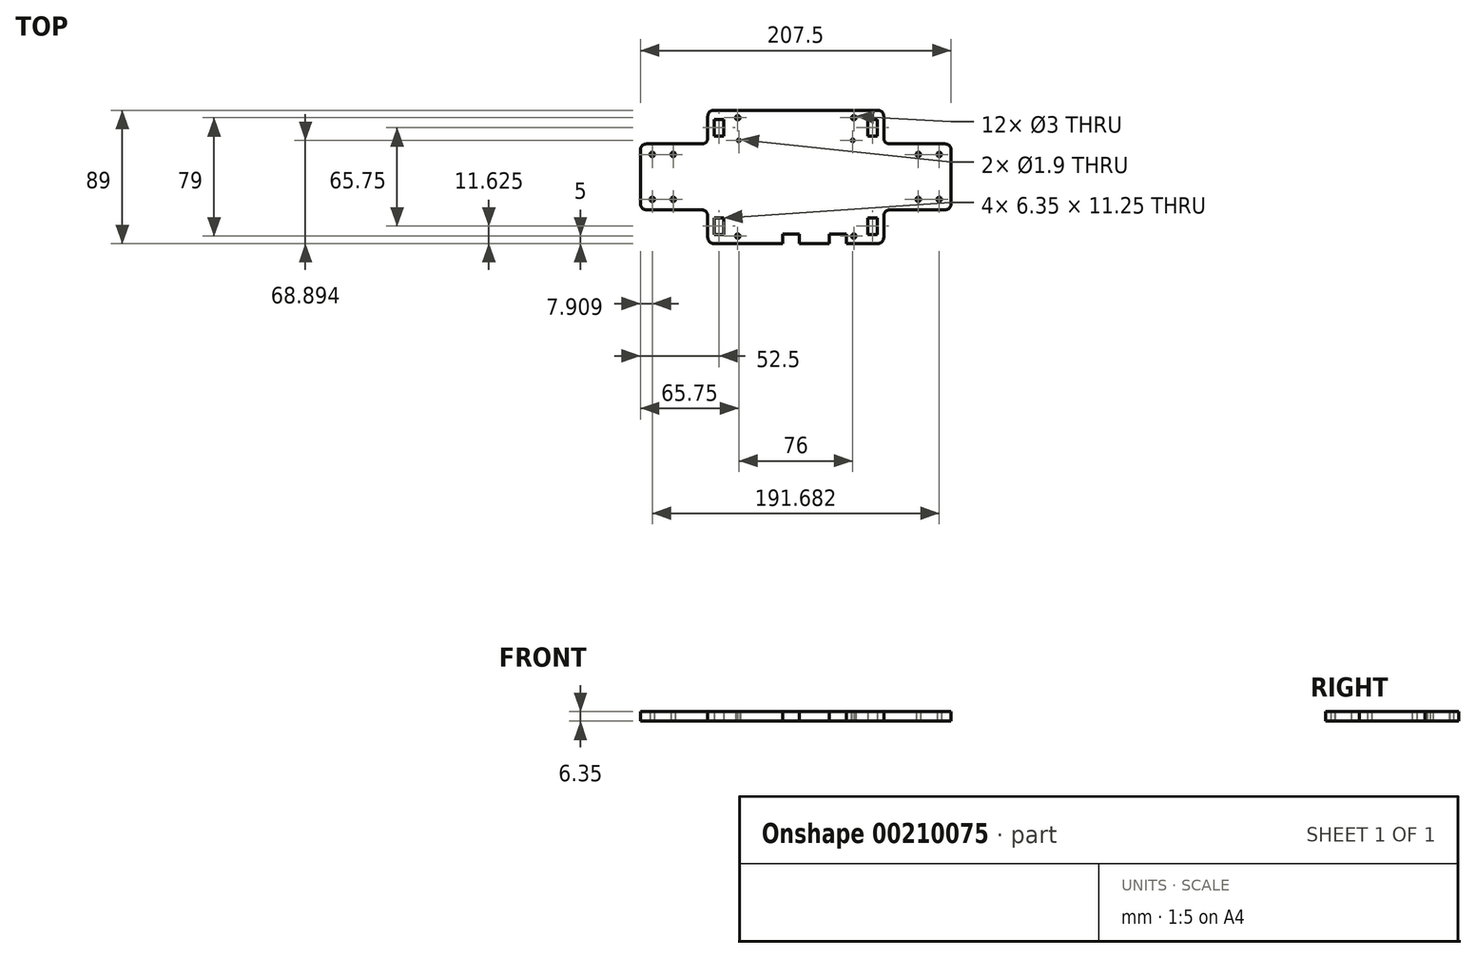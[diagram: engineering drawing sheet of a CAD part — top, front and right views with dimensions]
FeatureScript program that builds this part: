
annotation { "Feature Type Name" : "Feature", "Feature Type Description" : "" }
export const myFeature = defineFeature(function(context is Context, id is Id, definition is map)
    precondition{}
    {
        {
            var Q0;
            Q0=qCreatedBy(makeId("Top.planeOp"),FACE);
            var sketch = newSketch(context, id + "F0", { "sketchPlane" : qUnion([Q0])});
            skLineSegment(sketch, "E0.bottom", {"start": v(-54.75, 44.5) * mm, "end": v(103.75, 44.5) * mm});
            skLineSegment(sketch, "E0.top", {"start": v(-103.75, -44.5) * mm, "end": v(103.75, -44.5) * mm});
            skLineSegment(sketch, "E0.left", {"start": v(-103.75, 18) * mm, "end": v(-103.75, -44.5) * mm});
            skLineSegment(sketch, "E0.right", {"start": v(103.75, 44.5) * mm, "end": v(103.75, -44.5) * mm});
            skPoint(sketch, "E0.middle", {"position": v(0, 0) * mm});
            skLineSegment(sketch, "E1", {"start": v(-98.75, 44.5) * mm, "end": v(-98.75, -44.5) * mm});
            skLineSegment(sketch, "E2", {"start": v(-78.75, 44.5) * mm, "end": v(-78.75, -44.5) * mm});
            skLineSegment(sketch, "E3", {"start": v(-43.75, 44.5) * mm, "end": v(-43.75, -44.5) * mm});
            skLineSegment(sketch, "E4", {"start": v(43.75, 44.5) * mm, "end": v(43.75, -44.5) * mm});
            skLineSegment(sketch, "E5", {"start": v(78.75, 44.5) * mm, "end": v(78.75, -44.5) * mm});
            skLineSegment(sketch, "E6", {"start": v(98.75, 44.5) * mm, "end": v(98.75, -44.5) * mm});
            skLineSegment(sketch, "E7", {"start": v(-43.75, 31.5) * mm, "end": v(43.75, 31.5) * mm});
            skLineSegment(sketch, "E8", {"start": v(-43.75, -31.5) * mm, "end": v(43.75, -31.5) * mm});
            skLineSegment(sketch, "E9", {"start": v(-98.75, 22) * mm, "end": v(-78.75, 22) * mm});
            skLineSegment(sketch, "E10", {"start": v(-98.75, -22) * mm, "end": v(-78.75, -22) * mm});
            skLineSegment(sketch, "E11", {"start": v(78.75, 22) * mm, "end": v(98.75, 22) * mm});
            skLineSegment(sketch, "E12", {"start": v(78.75, -22) * mm, "end": v(98.75, -22) * mm});
            skPoint(sketch, "E13", {"position": v(38, 24.4) * mm});
            skPoint(sketch, "E14", {"position": v(-38, 24.4) * mm});
            skCircle(sketch, "E15", {"center": v(-38, 24.4) * mm, "radius": 0.95 * mm});
            skCircle(sketch, "E16", {"center": v(38, 24.4) * mm, "radius": 0.95 * mm});
            skPoint(sketch, "E17", {"position": v(-81.84, -15) * mm});
            skPoint(sketch, "E18", {"position": v(-81.84, 15) * mm});
            skPoint(sketch, "E19", {"position": v(-95.84, 15) * mm});
            skPoint(sketch, "E20", {"position": v(-95.84, -15) * mm});
            skPoint(sketch, "E21", {"position": v(81.84, -15) * mm});
            skPoint(sketch, "E22", {"position": v(95.84, -15) * mm});
            skPoint(sketch, "E23", {"position": v(95.84, 15) * mm});
            skPoint(sketch, "E24", {"position": v(81.84, 15) * mm});
            skCircle(sketch, "E25", {"center": v(-95.84, -15) * mm, "radius": 1.5 * mm});
            skCircle(sketch, "E26", {"center": v(-81.84, -15) * mm, "radius": 1.5 * mm});
            skCircle(sketch, "E27", {"center": v(-81.84, 15) * mm, "radius": 1.5 * mm});
            skCircle(sketch, "E28", {"center": v(-95.84, 15) * mm, "radius": 1.5 * mm});
            skCircle(sketch, "E29", {"center": v(81.84, 15) * mm, "radius": 1.5 * mm});
            skCircle(sketch, "E30", {"center": v(95.84, 15) * mm, "radius": 1.5 * mm});
            skCircle(sketch, "E31", {"center": v(95.84, -15) * mm, "radius": 1.5 * mm});
            skCircle(sketch, "E32", {"center": v(81.84, -15) * mm, "radius": 1.5 * mm});
            skLineSegment(sketch, "E33.bottom", {"start": v(-8.75, -38.15) * mm, "end": v(2.5, -38.15) * mm});
            skLineSegment(sketch, "E33.top", {"start": v(-8.75, -44.5) * mm, "end": v(2.5, -44.5) * mm});
            skLineSegment(sketch, "E33.left", {"start": v(-8.75, -38.15) * mm, "end": v(-8.75, -44.5) * mm});
            skLineSegment(sketch, "E33.right", {"start": v(2.5, -38.15) * mm, "end": v(2.5, -44.5) * mm});
            skLineSegment(sketch, "E34.bottom", {"start": v(22.5, -44.5) * mm, "end": v(33.75, -44.5) * mm});
            skLineSegment(sketch, "E34.top", {"start": v(22.5, -38.15) * mm, "end": v(33.75, -38.15) * mm});
            skLineSegment(sketch, "E34.left", {"start": v(22.5, -44.5) * mm, "end": v(22.5, -38.15) * mm});
            skLineSegment(sketch, "E34.right", {"start": v(33.75, -44.5) * mm, "end": v(33.75, -38.15) * mm});
            skLineSegment(sketch, "E35.bottom", {"start": v(48.08, -38.5) * mm, "end": v(54.43, -38.5) * mm});
            skLineSegment(sketch, "E35.top", {"start": v(48.08, -27.25) * mm, "end": v(54.43, -27.25) * mm});
            skLineSegment(sketch, "E35.left", {"start": v(48.08, -38.5) * mm, "end": v(48.08, -27.25) * mm});
            skLineSegment(sketch, "E35.right", {"start": v(54.43, -38.5) * mm, "end": v(54.43, -27.25) * mm});
            skLineSegment(sketch, "E36.bottom", {"start": v(48.08, 27.25) * mm, "end": v(54.43, 27.25) * mm});
            skLineSegment(sketch, "E36.top", {"start": v(48.08, 38.5) * mm, "end": v(54.43, 38.5) * mm});
            skLineSegment(sketch, "E36.left", {"start": v(48.08, 27.25) * mm, "end": v(48.08, 38.5) * mm});
            skLineSegment(sketch, "E36.right", {"start": v(54.43, 27.25) * mm, "end": v(54.43, 38.5) * mm});
            skLineSegment(sketch, "E37.bottom", {"start": v(-54.43, -38.5) * mm, "end": v(-48.08, -38.5) * mm});
            skLineSegment(sketch, "E37.top", {"start": v(-54.43, -27.25) * mm, "end": v(-48.08, -27.25) * mm});
            skLineSegment(sketch, "E37.left", {"start": v(-54.43, -38.5) * mm, "end": v(-54.43, -27.25) * mm});
            skLineSegment(sketch, "E37.right", {"start": v(-48.08, -38.5) * mm, "end": v(-48.08, -27.25) * mm});
            skLineSegment(sketch, "E38.bottom", {"start": v(-54.42, 27.25) * mm, "end": v(-48.07, 27.25) * mm});
            skLineSegment(sketch, "E38.top", {"start": v(-54.42, 38.5) * mm, "end": v(-48.07, 38.5) * mm});
            skLineSegment(sketch, "E38.left", {"start": v(-54.42, 27.25) * mm, "end": v(-54.42, 38.5) * mm});
            skLineSegment(sketch, "E38.right", {"start": v(-48.07, 27.25) * mm, "end": v(-48.07, 38.5) * mm});
            skLineSegment(sketch, "E39", {"start": v(-99.75, 22) * mm, "end": v(-62.75, 22) * mm});
            skLineSegment(sketch, "E40", {"start": v(-58.75, 26) * mm, "end": v(-58.75, 40.5) * mm});
            skLineSegment(sketch, "E41", {"start": v(-103.75, 0) * mm, "end": v(103.75, 0) * mm, "construction": true});
            skLineSegment(sketch, "E42", {"start": v(0, 44.5) * mm, "end": v(0, -44.5) * mm, "construction": true});
            skPoint(sketch, "E43.visualSharp", {"position": v(-58.75, 22) * mm});
            skArc(sketch, "E43.filletArc", {"start": v(-62.75, 22) * mm, "mid": v(-59.92, 23.17) * mm, "end": v(-58.75, 26) * mm});
            skPoint(sketch, "E44.newPointB", {"position": v(-103.75, 44.5) * mm});
            skArc(sketch, "E44.filletArc", {"start": v(-54.75, 44.5) * mm, "mid": v(-57.58, 43.33) * mm, "end": v(-58.75, 40.5) * mm});
            skPoint(sketch, "E45.newPointB", {"position": v(-103.75, 22) * mm});
            skArc(sketch, "E45.filletArc", {"start": v(-99.75, 22) * mm, "mid": v(-102.58, 20.83) * mm, "end": v(-103.75, 18) * mm});
            skArc(sketch, "E46.MirrorCS", {"start": v(-99.75, -22) * mm, "mid": v(-102.58, -20.83) * mm, "end": v(-103.75, -18) * mm});
            skLineSegment(sketch, "E47.MirrorCS", {"start": v(-58.75, -26) * mm, "end": v(-58.75, -40.5) * mm});
            skLineSegment(sketch, "E48.MirrorCS", {"start": v(-99.75, -22) * mm, "end": v(-62.75, -22) * mm});
            skArc(sketch, "E49.MirrorCS", {"start": v(-62.75, -22) * mm, "mid": v(-59.92, -23.17) * mm, "end": v(-58.75, -26) * mm});
            skArc(sketch, "E50.MirrorCS", {"start": v(-54.75, -44.5) * mm, "mid": v(-57.58, -43.33) * mm, "end": v(-58.75, -40.5) * mm});
            skArc(sketch, "E51.MirrorCS", {"start": v(54.75, -44.5) * mm, "mid": v(57.58, -43.33) * mm, "end": v(58.75, -40.5) * mm});
            skLineSegment(sketch, "E52.MirrorCS", {"start": v(58.75, -26) * mm, "end": v(58.75, -40.5) * mm});
            skArc(sketch, "E53.MirrorCS", {"start": v(62.75, -22) * mm, "mid": v(59.92, -23.17) * mm, "end": v(58.75, -26) * mm});
            skLineSegment(sketch, "E54.MirrorCS", {"start": v(99.75, -22) * mm, "end": v(62.75, -22) * mm});
            skLineSegment(sketch, "E55.MirrorCS", {"start": v(98.75, -22) * mm, "end": v(78.75, -22) * mm});
            skArc(sketch, "E56.MirrorCS", {"start": v(99.75, -22) * mm, "mid": v(102.58, -20.83) * mm, "end": v(103.75, -18) * mm});
            skArc(sketch, "E57.MirrorCS", {"start": v(54.75, 44.5) * mm, "mid": v(57.58, 43.33) * mm, "end": v(58.75, 40.5) * mm});
            skLineSegment(sketch, "E58.MirrorCS", {"start": v(99.75, 22) * mm, "end": v(62.75, 22) * mm});
            skLineSegment(sketch, "E59.MirrorCS", {"start": v(58.75, 26) * mm, "end": v(58.75, 40.5) * mm});
            skArc(sketch, "E60.MirrorCS", {"start": v(62.75, 22) * mm, "mid": v(59.92, 23.17) * mm, "end": v(58.75, 26) * mm});
            skArc(sketch, "E61.MirrorCS", {"start": v(99.75, 22) * mm, "mid": v(102.58, 20.83) * mm, "end": v(103.75, 18) * mm});
            skPoint(sketch, "E62", {"position": v(-38.75, 39.5) * mm});
            skPoint(sketch, "E63", {"position": v(38.75, 39.5) * mm});
            skPoint(sketch, "E64", {"position": v(38.75, -39.5) * mm});
            skPoint(sketch, "E65", {"position": v(-38.75, -39.5) * mm});
            skCircle(sketch, "E66", {"center": v(-38.75, 39.5) * mm, "radius": 1.5 * mm});
            skCircle(sketch, "E67", {"center": v(38.75, 39.5) * mm, "radius": 1.5 * mm});
            skCircle(sketch, "E68", {"center": v(38.75, -39.5) * mm, "radius": 1.5 * mm});
            skCircle(sketch, "E69", {"center": v(-38.75, -39.5) * mm, "radius": 1.5 * mm});
            skSolve(sketch);
        }
        {
            var Q0;
            {var subQ5=sQuery(id+"F0.wireOp",EDGE,"E7");Q0=makeQuery(id+"F0.imprint","IMPRINT",FACE,{"disambiguationData":[TD([[makeQuery(id+"F0.imprint","IMPRINT",EDGE,{"derivedFrom":subQ5}),1.0]])]});}
            var Q1;
            {var subQ0=sQuery(id+"F0.wireOp",EDGE,"E8");Q1=makeQuery(id+"F0.imprint","IMPRINT",FACE,{"disambiguationData":[TD([[makeQuery(id+"F0.imprint","IMPRINT",EDGE,{"derivedFrom":subQ0}),-1.0]])]});}
            var Q2;
            Q2=makeQuery(id+"F0.imprint","IMPRINT",FACE,{"disambiguationData":[TD([[makeQuery(id+"F0.imprint","IMPRINT",EDGE,{"derivedFrom":sQuery(id+"F0.wireOp",EDGE,"E37.bottom")}),-1.0]])]});
            var Q3;
            Q3=makeQuery(id+"F0.imprint","IMPRINT",FACE,{"disambiguationData":[TD([[makeQuery(id+"F0.imprint","IMPRINT",EDGE,{"derivedFrom":sQuery(id+"F0.wireOp",EDGE,"E35.bottom")}),-1.0]])]});
            var Q4;
            {var subQ1=sQuery(id+"F0.wireOp",EDGE,"E7");Q4=makeQuery(id+"F0.imprint","IMPRINT",FACE,{"disambiguationData":[TD([[makeQuery(id+"F0.imprint","IMPRINT",EDGE,{"derivedFrom":subQ1}),-1.0]])]});}
            var Q5;
            Q5=makeQuery(id+"F0.imprint","IMPRINT",FACE,{"disambiguationData":[TD([[makeQuery(id+"F0.imprint","IMPRINT",EDGE,{"derivedFrom":sQuery(id+"F0.wireOp",EDGE,"E25")}),-1.0]])]});
            var Q6;
            Q6=makeQuery(id+"F0.imprint","IMPRINT",FACE,{"disambiguationData":[TD([[makeQuery(id+"F0.imprint","IMPRINT",EDGE,{"derivedFrom":sQuery(id+"F0.wireOp",EDGE,"E29")}),-1.0]])]});
            var Q7;
            {var subQ0=sQuery(id+"F0.wireOp",EDGE,"E45.filletArc");Q7=makeQuery(id+"F0.imprint","IMPRINT",FACE,{"disambiguationData":[TD([[makeQuery(id+"F0.imprint","IMPRINT",EDGE,{"derivedFrom":subQ0}),1.0]])]});}
            var Q8;
            {var subQ0=sQuery(id+"F0.wireOp",EDGE,"E56.MirrorCS");Q8=makeQuery(id+"F0.imprint","IMPRINT",FACE,{"disambiguationData":[TD([[makeQuery(id+"F0.imprint","IMPRINT",EDGE,{"derivedFrom":subQ0}),1.0]])]});}
            extrude(context, id + "F1", {"entities" : qUnion([Q0, Q1, Q2, Q3, Q4, Q5, Q6, Q7, Q8]), "depth" : 6.35 * mm});
        }
    });
